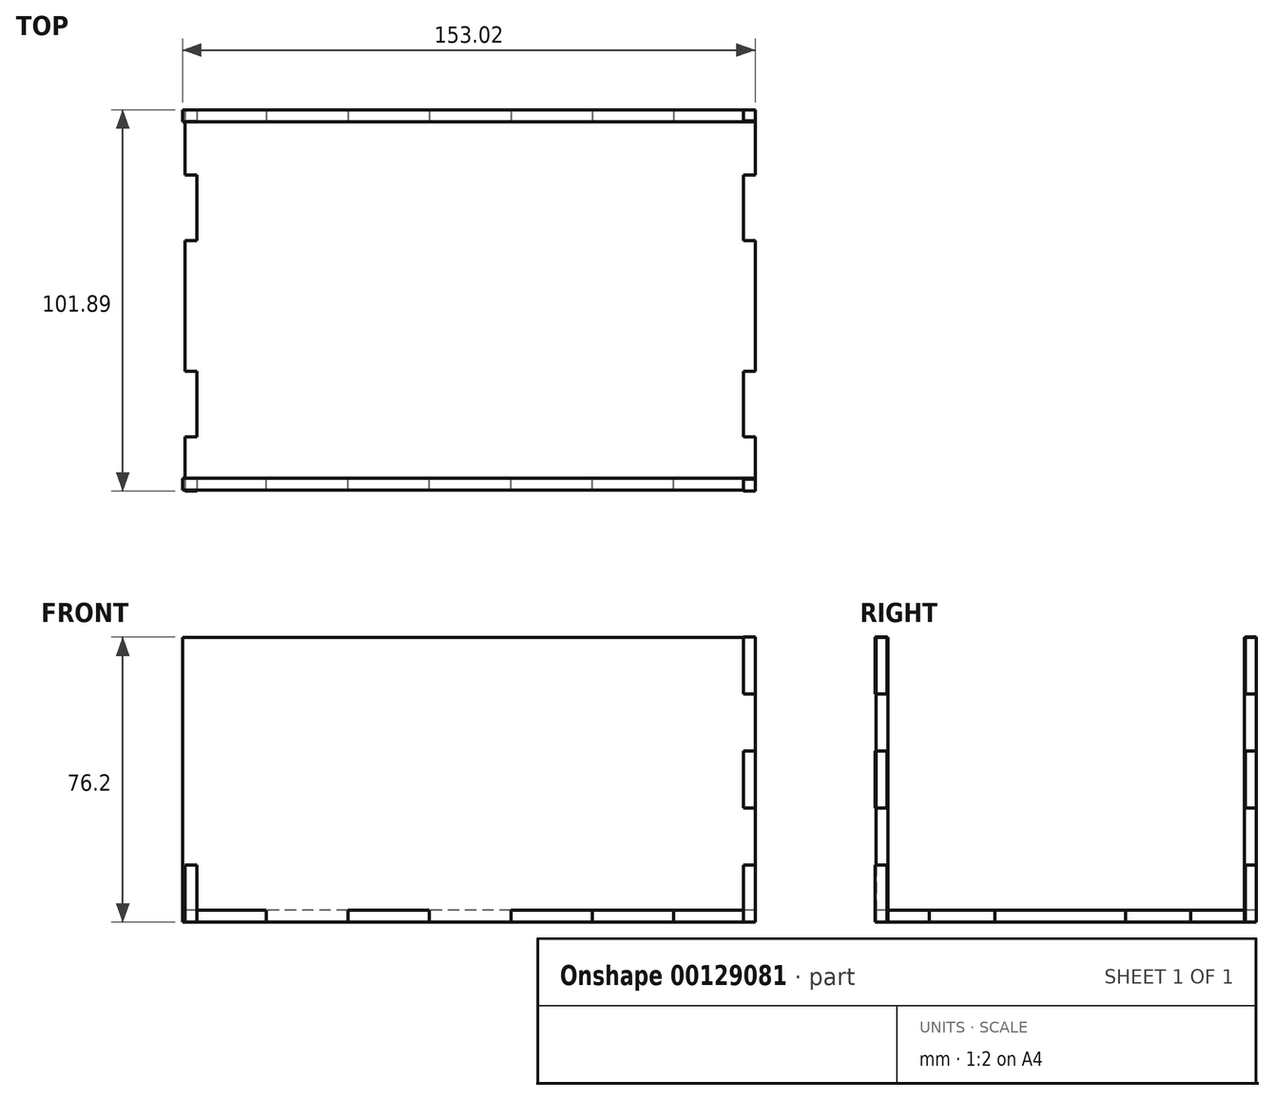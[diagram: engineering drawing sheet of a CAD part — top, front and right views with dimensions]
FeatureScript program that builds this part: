
annotation { "Feature Type Name" : "Feature", "Feature Type Description" : "" }
export const myFeature = defineFeature(function(context is Context, id is Id, definition is map)
    precondition{}
    {
        {
            var Q0;
            Q0=qCreatedBy(makeId("Top.planeOp"),FACE);
            var sketch = newSketch(context, id + "F0", { "sketchPlane" : qUnion([Q0])});
            skLineSegment(sketch, "E0.bottom", {"start": v(76.2, 50.8) * mm, "end": v(-76.2, 50.8) * mm});
            skLineSegment(sketch, "E0.top", {"start": v(76.2, -50.8) * mm, "end": v(-76.2, -50.8) * mm});
            skLineSegment(sketch, "E0.left", {"start": v(76.2, 50.8) * mm, "end": v(76.2, -50.8) * mm});
            skLineSegment(sketch, "E0.right", {"start": v(-76.2, 50.8) * mm, "end": v(-76.2, -50.8) * mm});
            skPoint(sketch, "E0.middle", {"position": v(0, 0) * mm});
            skLineSegment(sketch, "E1", {"start": v(-76.2, 50.8) * mm, "end": v(-73.03, 50.8) * mm});
            skLineSegment(sketch, "E2.0.1.0", {"start": v(-76.2, 33.33) * mm, "end": v(-73.03, 33.33) * mm});
            skLineSegment(sketch, "E2.0.2.0", {"start": v(-76.2, 15.85) * mm, "end": v(-73.03, 15.85) * mm});
            skLineSegment(sketch, "E2.0.3.0", {"start": v(-76.2, -1.62) * mm, "end": v(-73.03, -1.62) * mm});
            skLineSegment(sketch, "E2.0.4.0", {"start": v(-76.2, -19.1) * mm, "end": v(-73.03, -19.1) * mm});
            skLineSegment(sketch, "E2.0.5.0", {"start": v(-76.2, -36.57) * mm, "end": v(-73.02, -36.57) * mm});
            skLineSegment(sketch, "E2.direction1", {"start": v(-76.2, 50.8) * mm, "end": v(-50.8, 50.8) * mm, "construction": true});
            skLineSegment(sketch, "E2.direction2", {"start": v(-76.2, 50.8) * mm, "end": v(-76.2, 33.33) * mm, "construction": true});
            skLineSegment(sketch, "E3", {"start": v(-73.03, 50.8) * mm, "end": v(-73.03, -50.8) * mm});
            skLineSegment(sketch, "E4.MirrorCS", {"start": v(76.2, 50.8) * mm, "end": v(73.03, 50.8) * mm});
            skLineSegment(sketch, "E5.MirrorCS", {"start": v(76.2, 33.33) * mm, "end": v(73.03, 33.33) * mm});
            skLineSegment(sketch, "E6.MirrorCS", {"start": v(76.2, 15.85) * mm, "end": v(73.03, 15.85) * mm});
            skLineSegment(sketch, "E7.MirrorCS", {"start": v(76.2, -36.57) * mm, "end": v(73.02, -36.57) * mm});
            skLineSegment(sketch, "E8.MirrorCS", {"start": v(76.2, -1.62) * mm, "end": v(73.03, -1.62) * mm});
            skLineSegment(sketch, "E9.MirrorCS", {"start": v(76.2, -19.1) * mm, "end": v(73.03, -19.1) * mm});
            skLineSegment(sketch, "E10.MirrorCS", {"start": v(76.2, 50.8) * mm, "end": v(76.2, 33.33) * mm, "construction": true});
            skLineSegment(sketch, "E11.MirrorCS", {"start": v(73.03, 50.8) * mm, "end": v(73.03, -50.8) * mm});
            skLineSegment(sketch, "E12", {"start": v(-76.2, 50.8) * mm, "end": v(-76.2, 47.62) * mm});
            skLineSegment(sketch, "E13.1.0.0", {"start": v(-54.43, 50.8) * mm, "end": v(-54.43, 47.62) * mm});
            skLineSegment(sketch, "E13.2.0.0", {"start": v(-32.66, 50.8) * mm, "end": v(-32.66, 47.62) * mm});
            skLineSegment(sketch, "E13.3.0.0", {"start": v(-10.89, 50.8) * mm, "end": v(-10.89, 47.62) * mm});
            skLineSegment(sketch, "E13.4.0.0", {"start": v(10.89, 50.8) * mm, "end": v(10.89, 47.62) * mm});
            skLineSegment(sketch, "E13.5.0.0", {"start": v(32.66, 50.8) * mm, "end": v(32.66, 47.62) * mm});
            skLineSegment(sketch, "E13.6.0.0", {"start": v(54.43, 50.8) * mm, "end": v(54.43, 47.62) * mm});
            skLineSegment(sketch, "E13.7.0.0", {"start": v(76.2, 50.8) * mm, "end": v(76.2, 47.62) * mm});
            skLineSegment(sketch, "E13.direction1", {"start": v(-76.2, 47.62) * mm, "end": v(-54.43, 47.62) * mm, "construction": true});
            skLineSegment(sketch, "E14", {"start": v(-76.2, 47.62) * mm, "end": v(76.2, 47.62) * mm});
            skLineSegment(sketch, "E15.MirrorCS", {"start": v(-76.2, -50.8) * mm, "end": v(-73.03, -50.8) * mm});
            skLineSegment(sketch, "E16.MirrorCS", {"start": v(-76.2, -50.8) * mm, "end": v(-76.2, -47.62) * mm});
            skLineSegment(sketch, "E17.MirrorCS", {"start": v(76.2, -50.8) * mm, "end": v(76.2, -47.62) * mm});
            skLineSegment(sketch, "E18.MirrorCS", {"start": v(76.2, -50.8) * mm, "end": v(73.03, -50.8) * mm});
            skLineSegment(sketch, "E19.MirrorCS", {"start": v(-54.43, -50.8) * mm, "end": v(-54.43, -47.62) * mm});
            skLineSegment(sketch, "E20.MirrorCS", {"start": v(54.43, -50.8) * mm, "end": v(54.43, -47.62) * mm});
            skLineSegment(sketch, "E21.MirrorCS", {"start": v(-32.66, -50.8) * mm, "end": v(-32.66, -47.62) * mm});
            skLineSegment(sketch, "E22.MirrorCS", {"start": v(10.89, -50.8) * mm, "end": v(10.89, -47.62) * mm});
            skLineSegment(sketch, "E23.MirrorCS", {"start": v(32.66, -50.8) * mm, "end": v(32.66, -47.62) * mm});
            skLineSegment(sketch, "E24.MirrorCS", {"start": v(-10.89, -50.8) * mm, "end": v(-10.89, -47.62) * mm});
            skLineSegment(sketch, "E25.MirrorCS", {"start": v(-76.2, -47.62) * mm, "end": v(76.2, -47.62) * mm});
            skLineSegment(sketch, "E26.MirrorCS", {"start": v(-76.2, -47.62) * mm, "end": v(-54.43, -47.62) * mm, "construction": true});
            skLineSegment(sketch, "E27.MirrorCS", {"start": v(-76.2, -50.8) * mm, "end": v(-50.8, -50.8) * mm, "construction": true});
            skSolve(sketch);
        }
        {
            var Q0;
            {var subQ3=sQuery(id+"F0.wireOp",EDGE,"E13.1.0.0");Q0=makeQuery(id+"F0.imprint","IMPRINT",FACE,{"disambiguationData":[TD([[makeQuery(id+"F0.imprint","IMPRINT",EDGE,{"derivedFrom":subQ3}),-1.0]])]});}
            var Q1;
            {var subQ0=sQuery(id+"F0.wireOp",EDGE,"E1");Q1=makeQuery(id+"F0.imprint","IMPRINT",FACE,{"disambiguationData":[TD([[makeQuery(id+"F0.imprint","IMPRINT",EDGE,{"derivedFrom":subQ0}),-1.0]])]});}
            var Q2;
            {var subQ3=sQuery(id+"F0.wireOp",EDGE,"E2.0.1.0");Q2=makeQuery(id+"F0.imprint","IMPRINT",FACE,{"disambiguationData":[TD([[makeQuery(id+"F0.imprint","IMPRINT",EDGE,{"derivedFrom":subQ3}),1.0]])]});}
            var Q3;
            {var subQ0=sQuery(id+"F0.wireOp",EDGE,"E2.0.2.0");Q3=makeQuery(id+"F0.imprint","IMPRINT",FACE,{"disambiguationData":[TD([[makeQuery(id+"F0.imprint","IMPRINT",EDGE,{"derivedFrom":subQ0}),-1.0]])]});}
            var Q4;
            {var subQ0=sQuery(id+"F0.wireOp",EDGE,"E2.0.3.0");Q4=makeQuery(id+"F0.imprint","IMPRINT",FACE,{"disambiguationData":[TD([[makeQuery(id+"F0.imprint","IMPRINT",EDGE,{"derivedFrom":subQ0}),-1.0]])]});}
            var Q5;
            {var subQ3=sQuery(id+"F0.wireOp",EDGE,"E2.0.5.0");Q5=makeQuery(id+"F0.imprint","IMPRINT",FACE,{"disambiguationData":[TD([[makeQuery(id+"F0.imprint","IMPRINT",EDGE,{"derivedFrom":subQ3}),-1.0]])]});}
            var Q6;
            {var subQ5=sQuery(id+"F0.wireOp",EDGE,"E16.MirrorCS");Q6=makeQuery(id+"F0.imprint","IMPRINT",FACE,{"disambiguationData":[TD([[makeQuery(id+"F0.imprint","IMPRINT",EDGE,{"derivedFrom":subQ5}),-1.0]])]});}
            var Q7;
            {var subQ5=sQuery(id+"F0.wireOp",EDGE,"E19.MirrorCS");Q7=makeQuery(id+"F0.imprint","IMPRINT",FACE,{"disambiguationData":[TD([[makeQuery(id+"F0.imprint","IMPRINT",EDGE,{"derivedFrom":subQ5}),1.0]])]});}
            var Q8;
            {var subQ0=sQuery(id+"F0.wireOp",EDGE,"E21.MirrorCS");Q8=makeQuery(id+"F0.imprint","IMPRINT",FACE,{"disambiguationData":[TD([[makeQuery(id+"F0.imprint","IMPRINT",EDGE,{"derivedFrom":subQ0}),-1.0]])]});}
            var Q9;
            {var subQ0=sQuery(id+"F0.wireOp",EDGE,"E22.MirrorCS");Q9=makeQuery(id+"F0.imprint","IMPRINT",FACE,{"disambiguationData":[TD([[makeQuery(id+"F0.imprint","IMPRINT",EDGE,{"derivedFrom":subQ0}),-1.0]])]});}
            var Q10;
            {var subQ5=sQuery(id+"F0.wireOp",EDGE,"E20.MirrorCS");Q10=makeQuery(id+"F0.imprint","IMPRINT",FACE,{"disambiguationData":[TD([[makeQuery(id+"F0.imprint","IMPRINT",EDGE,{"derivedFrom":subQ5}),-1.0]])]});}
            var Q11;
            {var subQ0=sQuery(id+"F0.wireOp",EDGE,"E7.MirrorCS");Q11=makeQuery(id+"F0.imprint","IMPRINT",FACE,{"disambiguationData":[TD([[makeQuery(id+"F0.imprint","IMPRINT",EDGE,{"derivedFrom":subQ0}),1.0]])]});}
            var Q12;
            {var subQ0=sQuery(id+"F0.wireOp",EDGE,"E8.MirrorCS");Q12=makeQuery(id+"F0.imprint","IMPRINT",FACE,{"disambiguationData":[TD([[makeQuery(id+"F0.imprint","IMPRINT",EDGE,{"derivedFrom":subQ0}),1.0]])]});}
            var Q13;
            {var subQ0=sQuery(id+"F0.wireOp",EDGE,"E6.MirrorCS");Q13=makeQuery(id+"F0.imprint","IMPRINT",FACE,{"disambiguationData":[TD([[makeQuery(id+"F0.imprint","IMPRINT",EDGE,{"derivedFrom":subQ0}),1.0]])]});}
            var Q14;
            {var subQ0=sQuery(id+"F0.wireOp",EDGE,"E5.MirrorCS");Q14=makeQuery(id+"F0.imprint","IMPRINT",FACE,{"disambiguationData":[TD([[makeQuery(id+"F0.imprint","IMPRINT",EDGE,{"derivedFrom":subQ0}),-1.0]])]});}
            var Q15;
            {var subQ0=sQuery(id+"F0.wireOp",EDGE,"E4.MirrorCS");Q15=makeQuery(id+"F0.imprint","IMPRINT",FACE,{"disambiguationData":[TD([[makeQuery(id+"F0.imprint","IMPRINT",EDGE,{"derivedFrom":subQ0}),1.0]])]});}
            var Q16;
            {var subQ3=sQuery(id+"F0.wireOp",EDGE,"E13.6.0.0");Q16=makeQuery(id+"F0.imprint","IMPRINT",FACE,{"disambiguationData":[TD([[makeQuery(id+"F0.imprint","IMPRINT",EDGE,{"derivedFrom":subQ3}),1.0]])]});}
            var Q17;
            {var subQ0=sQuery(id+"F0.wireOp",EDGE,"E13.4.0.0");Q17=makeQuery(id+"F0.imprint","IMPRINT",FACE,{"disambiguationData":[TD([[makeQuery(id+"F0.imprint","IMPRINT",EDGE,{"derivedFrom":subQ0}),1.0]])]});}
            var Q18;
            {var subQ0=sQuery(id+"F0.wireOp",EDGE,"E13.2.0.0");Q18=makeQuery(id+"F0.imprint","IMPRINT",FACE,{"disambiguationData":[TD([[makeQuery(id+"F0.imprint","IMPRINT",EDGE,{"derivedFrom":subQ0}),1.0]])]});}
            var Q19;
            {var subQ6=sQuery(id+"F0.wireOp",EDGE,"E3");var subQ25=makeQuery(id+"F0.imprint","INTERSECT",VERTEX,{"derivedFrom":[sQuery(id+"F0.wireOp",EDGE,"E2.0.1.0"),subQ6]});Q19=makeQuery(id+"F0.imprint","IMPRINT",FACE,{"disambiguationData":[TD([[makeQuery(id+"F0.imprint","IMPRINT",EDGE,{"disambiguationData":[TD([[subQ25,1.0]])],"derivedFrom":subQ6}),1.0]])]});}
            extrude(context, id + "F1", {"entities" : qUnion([Q0, Q1, Q2, Q3, Q4, Q5, Q6, Q7, Q8, Q9, Q10, Q11, Q12, Q13, Q14, Q15, Q16, Q17, Q18, Q19]), "depth" : 3.17 * mm});
        }
        {
            var Q0;
            {var subQ0=sQuery(id+"F0.wireOp",EDGE,"E0.left");Q0=makeQuery(id+"F1.opExtrude","SWEPT_FACE",FACE,{"disambiguationData":[OSD([subQ0]),TDD([makeQuery(id+"F0.imprint","IMPRINT",EDGE,{"disambiguationData":[TD([[makeQuery(id+"F0.imprint","INTERSECT",VERTEX,{"derivedFrom":[sQuery(id+"F0.wireOp",EDGE,"E7.MirrorCS"),subQ0]}),-1.0]])],"derivedFrom":subQ0})])]});}
            var sketch = newSketch(context, id + "F2", { "sketchPlane" : qUnion([Q0])});
            skLineSegment(sketch, "E28.bottom", {"start": v(50.8, 0) * mm, "end": v(-51.09, 0) * mm});
            skLineSegment(sketch, "E28.top", {"start": v(50.8, 76.2) * mm, "end": v(-51.09, 76.2) * mm});
            skLineSegment(sketch, "E28.left", {"start": v(50.8, 0) * mm, "end": v(50.8, 76.2) * mm});
            skLineSegment(sketch, "E28.right", {"start": v(-51.09, 0) * mm, "end": v(-51.09, 76.2) * mm});
            skLineSegment(sketch, "E29", {"start": v(-51.09, 76.2) * mm, "end": v(-47.91, 76.2) * mm});
            skLineSegment(sketch, "E30.0.1.0", {"start": v(-51.09, 60.96) * mm, "end": v(-47.91, 60.96) * mm});
            skLineSegment(sketch, "E30.0.2.0", {"start": v(-51.09, 45.72) * mm, "end": v(-47.91, 45.72) * mm});
            skLineSegment(sketch, "E30.0.3.0", {"start": v(-51.09, 30.48) * mm, "end": v(-47.91, 30.48) * mm});
            skLineSegment(sketch, "E30.0.4.0", {"start": v(-51.09, 15.24) * mm, "end": v(-47.91, 15.24) * mm});
            skLineSegment(sketch, "E30.0.5.0", {"start": v(-51.09, 0) * mm, "end": v(-47.91, 0) * mm});
            skLineSegment(sketch, "E30.direction1", {"start": v(-51.09, 76.2) * mm, "end": v(-25.69, 76.2) * mm, "construction": true});
            skLineSegment(sketch, "E30.direction2", {"start": v(-51.09, 76.2) * mm, "end": v(-51.09, 60.96) * mm, "construction": true});
            skLineSegment(sketch, "E31", {"start": v(-47.91, 0) * mm, "end": v(-47.91, 76.2) * mm});
            skLineSegment(sketch, "E32.MirrorCS", {"start": v(51.09, 76.2) * mm, "end": v(47.91, 76.2) * mm});
            skLineSegment(sketch, "E33.MirrorCS", {"start": v(51.09, 0) * mm, "end": v(47.91, 0) * mm});
            skLineSegment(sketch, "E34.MirrorCS", {"start": v(51.09, 45.72) * mm, "end": v(47.91, 45.72) * mm});
            skLineSegment(sketch, "E35.MirrorCS", {"start": v(51.09, 60.96) * mm, "end": v(47.91, 60.96) * mm});
            skLineSegment(sketch, "E36.MirrorCS", {"start": v(51.09, 30.48) * mm, "end": v(47.91, 30.48) * mm});
            skLineSegment(sketch, "E37.MirrorCS", {"start": v(51.09, 15.24) * mm, "end": v(47.91, 15.24) * mm});
            skLineSegment(sketch, "E38.MirrorCS", {"start": v(51.09, 0) * mm, "end": v(51.09, 76.2) * mm});
            skLineSegment(sketch, "E39.MirrorCS", {"start": v(47.91, 0) * mm, "end": v(47.91, 76.2) * mm});
            skLineSegment(sketch, "E40.MirrorCS", {"start": v(51.09, 76.2) * mm, "end": v(51.09, 60.96) * mm, "construction": true});
            skSolve(sketch);
        }
        {
            var Q0;
            {var subQ0=sQuery(id+"F2.wireOp",EDGE,"E29");Q0=makeQuery(id+"F2.imprint","IMPRINT",FACE,{"disambiguationData":[TD([[makeQuery(id+"F2.imprint","IMPRINT",EDGE,{"derivedFrom":subQ0}),-1.0]])]});}
            var Q1;
            {var subQ0=sQuery(id+"F2.wireOp",EDGE,"E30.0.2.0");Q1=makeQuery(id+"F2.imprint","IMPRINT",FACE,{"disambiguationData":[TD([[makeQuery(id+"F2.imprint","IMPRINT",EDGE,{"derivedFrom":subQ0}),-1.0]])]});}
            var Q2;
            {var subQ2=sQuery(id+"F2.wireOp",EDGE,"E30.0.4.0");Q2=makeQuery(id+"F2.imprint","IMPRINT",FACE,{"disambiguationData":[TD([[makeQuery(id+"F2.imprint","IMPRINT",EDGE,{"derivedFrom":subQ2}),-1.0]])]});}
            var Q3;
            {var subQ0=sQuery(id+"F2.wireOp",EDGE,"E36.MirrorCS");var subQ1=sQuery(id+"F2.wireOp",EDGE,"E28.left");var subQ2=makeQuery(id+"F2.imprint","INTERSECT",VERTEX,{"derivedFrom":[subQ1,subQ0]});Q3=makeQuery(id+"F2.imprint","IMPRINT",FACE,{"disambiguationData":[TD([[makeQuery(id+"F2.imprint","IMPRINT",EDGE,{"disambiguationData":[TD([[subQ2,-1.0]])],"derivedFrom":subQ1}),1.0]])]});}
            var Q4;
            {var subQ0=sQuery(id+"F2.wireOp",EDGE,"E33.MirrorCS");var subQ1=sQuery(id+"F2.wireOp",EDGE,"E28.left");var subQ2=makeQuery(id+"F2.imprint","INTERSECT",VERTEX,{"derivedFrom":[subQ1,subQ0]});Q4=makeQuery(id+"F2.imprint","IMPRINT",FACE,{"disambiguationData":[TD([[makeQuery(id+"F2.imprint","IMPRINT",EDGE,{"disambiguationData":[TD([[subQ2,-1.0]])],"derivedFrom":subQ1}),1.0]])]});}
            var Q5;
            {var subQ0=sQuery(id+"F2.wireOp",EDGE,"E32.MirrorCS");var subQ1=sQuery(id+"F2.wireOp",EDGE,"E28.left");var subQ2=makeQuery(id+"F2.imprint","INTERSECT",VERTEX,{"derivedFrom":[subQ1,subQ0]});Q5=makeQuery(id+"F2.imprint","IMPRINT",FACE,{"disambiguationData":[TD([[makeQuery(id+"F2.imprint","IMPRINT",EDGE,{"disambiguationData":[TD([[subQ2,1.0]])],"derivedFrom":subQ1}),1.0]])]});}
            var Q6;
            {var subQ4=sQuery(id+"F2.wireOp",EDGE,"E28.top");Q6=makeQuery(id+"F2.imprint","IMPRINT",FACE,{"disambiguationData":[TD([[makeQuery(id+"F2.imprint","IMPRINT",EDGE,{"derivedFrom":subQ4}),1.0]])]});}
            extrude(context, id + "F3", {"entities" : qUnion([Q0, Q1, Q2, Q3, Q4, Q5, Q6]), "operationType" : NewBodyOperationType.ADD, "oppositeDirection" : true, "depth" : 3.17 * mm});
        }
        {
            var Q0;
            Q0=makeQuery(id+"F1.opExtrude","SWEPT_BODY",BODY,{"disambiguationData":[OSD([sQuery(id+"F0.wireOp",EDGE,"E0.bottom"),sQuery(id+"F0.wireOp",EDGE,"E0.right"),sQuery(id+"F0.wireOp",EDGE,"E1"),sQuery(id+"F0.wireOp",EDGE,"E2.0.1.0"),sQuery(id+"F0.wireOp",EDGE,"E2.0.2.0"),sQuery(id+"F0.wireOp",EDGE,"E2.0.4.0"),sQuery(id+"F0.wireOp",EDGE,"E2.0.5.0"),sQuery(id+"F0.wireOp",EDGE,"E3"),sQuery(id+"F0.wireOp",EDGE,"E4.MirrorCS"),sQuery(id+"F0.wireOp",EDGE,"E5.MirrorCS"),sQuery(id+"F0.wireOp",EDGE,"E6.MirrorCS"),sQuery(id+"F0.wireOp",EDGE,"E7.MirrorCS"),sQuery(id+"F0.wireOp",EDGE,"E9.MirrorCS"),sQuery(id+"F0.wireOp",EDGE,"E0.left"),sQuery(id+"F0.wireOp",EDGE,"E11.MirrorCS"),sQuery(id+"F0.wireOp",EDGE,"E12"),sQuery(id+"F0.wireOp",EDGE,"E13.1.0.0"),sQuery(id+"F0.wireOp",EDGE,"E13.2.0.0"),sQuery(id+"F0.wireOp",EDGE,"E13.3.0.0"),sQuery(id+"F0.wireOp",EDGE,"E13.4.0.0"),sQuery(id+"F0.wireOp",EDGE,"E13.5.0.0"),sQuery(id+"F0.wireOp",EDGE,"E13.6.0.0"),sQuery(id+"F0.wireOp",EDGE,"E13.7.0.0"),sQuery(id+"F0.wireOp",EDGE,"E14"),sQuery(id+"F0.wireOp",EDGE,"E16.MirrorCS"),sQuery(id+"F0.wireOp",EDGE,"E19.MirrorCS"),sQuery(id+"F0.wireOp",EDGE,"E20.MirrorCS"),sQuery(id+"F0.wireOp",EDGE,"E21.MirrorCS"),sQuery(id+"F0.wireOp",EDGE,"E22.MirrorCS"),sQuery(id+"F0.wireOp",EDGE,"E23.MirrorCS"),sQuery(id+"F0.wireOp",EDGE,"E24.MirrorCS"),sQuery(id+"F0.wireOp",EDGE,"E25.MirrorCS"),sQuery(id+"F0.wireOp",EDGE,"E0.top")])]});
            var Q1;
            Q1=qCreatedBy(makeId("Right.planeOp"),FACE);
            mirror(context, id + "F4", {"entities" : qUnion([Q0]), "mirrorPlane" : qUnion([Q1])});
        }
        {
            var Q0;
            {var subQ0=sQuery(id+"F0.wireOp",EDGE,"E14");Q0=makeQuery(id+"F4.opPattern","COPY",FACE,{"derivedFrom":makeQuery(id+"F1.opExtrude","SWEPT_FACE",FACE,{"disambiguationData":[OSD([subQ0]),TDD([makeQuery(id+"F0.imprint","IMPRINT",EDGE,{"disambiguationData":[TD([[makeQuery(id+"F0.imprint","INTERSECT",VERTEX,{"derivedFrom":[sQuery(id+"F0.wireOp",EDGE,"E13.1.0.0"),subQ0]}),-1.0]])],"derivedFrom":subQ0})])]}),"instanceName":"1"});}
            var sketch = newSketch(context, id + "F5", { "sketchPlane" : qUnion([Q0])});
            skLineSegment(sketch, "E41.bottom", {"start": v(-76.2, 0) * mm, "end": v(76.82, 0) * mm});
            skLineSegment(sketch, "E41.top", {"start": v(-76.2, 76.14) * mm, "end": v(76.82, 76.14) * mm});
            skLineSegment(sketch, "E41.left", {"start": v(-76.2, 0) * mm, "end": v(-76.2, 76.14) * mm});
            skLineSegment(sketch, "E41.right", {"start": v(76.82, 0) * mm, "end": v(76.82, 76.14) * mm});
            skSolve(sketch);
        }
        {
            var Q0;
            Q0=makeQuery(id+"F5.imprint","IMPRINT",FACE,{"disambiguationData":[TD([[makeQuery(id+"F5.imprint","IMPRINT",EDGE,{"derivedFrom":sQuery(id+"F5.wireOp",EDGE,"E41.top")}),-1.0]])]});
            extrude(context, id + "F6", {"entities" : qUnion([Q0]), "depth" : 3.17 * mm});
        }
        {
            var Q0;
            Q0=makeQuery(id+"F6.opExtrude","SWEPT_BODY",BODY,{"disambiguationData":[OSD([sQuery(id+"F0.wireOp",EDGE,"E13.1.0.0"),sQuery(id+"F0.wireOp",EDGE,"E13.2.0.0"),sQuery(id+"F0.wireOp",EDGE,"E14"),sQuery(id+"F5.wireOp",EDGE,"E41.bottom"),sQuery(id+"F5.wireOp",EDGE,"E41.top"),sQuery(id+"F5.wireOp",EDGE,"E41.left"),sQuery(id+"F5.wireOp",EDGE,"E41.right")])]});
            var Q1;
            Q1=qCreatedBy(makeId("Front.planeOp"),FACE);
            mirror(context, id + "F7", {"entities" : qUnion([Q0]), "mirrorPlane" : qUnion([Q1])});
        }
        {
            var Q0;
            Q0=makeQuery(id+"F1.opExtrude","SWEPT_BODY",BODY,{"disambiguationData":[OSD([sQuery(id+"F0.wireOp",EDGE,"E0.bottom"),sQuery(id+"F0.wireOp",EDGE,"E0.right"),sQuery(id+"F0.wireOp",EDGE,"E1"),sQuery(id+"F0.wireOp",EDGE,"E2.0.1.0"),sQuery(id+"F0.wireOp",EDGE,"E2.0.2.0"),sQuery(id+"F0.wireOp",EDGE,"E2.0.4.0"),sQuery(id+"F0.wireOp",EDGE,"E2.0.5.0"),sQuery(id+"F0.wireOp",EDGE,"E3"),sQuery(id+"F0.wireOp",EDGE,"E4.MirrorCS"),sQuery(id+"F0.wireOp",EDGE,"E5.MirrorCS"),sQuery(id+"F0.wireOp",EDGE,"E6.MirrorCS"),sQuery(id+"F0.wireOp",EDGE,"E7.MirrorCS"),sQuery(id+"F0.wireOp",EDGE,"E9.MirrorCS"),sQuery(id+"F0.wireOp",EDGE,"E0.left"),sQuery(id+"F0.wireOp",EDGE,"E11.MirrorCS"),sQuery(id+"F0.wireOp",EDGE,"E12"),sQuery(id+"F0.wireOp",EDGE,"E13.1.0.0"),sQuery(id+"F0.wireOp",EDGE,"E13.2.0.0"),sQuery(id+"F0.wireOp",EDGE,"E13.3.0.0"),sQuery(id+"F0.wireOp",EDGE,"E13.4.0.0"),sQuery(id+"F0.wireOp",EDGE,"E13.5.0.0"),sQuery(id+"F0.wireOp",EDGE,"E13.6.0.0"),sQuery(id+"F0.wireOp",EDGE,"E13.7.0.0"),sQuery(id+"F0.wireOp",EDGE,"E14"),sQuery(id+"F0.wireOp",EDGE,"E16.MirrorCS"),sQuery(id+"F0.wireOp",EDGE,"E19.MirrorCS"),sQuery(id+"F0.wireOp",EDGE,"E20.MirrorCS"),sQuery(id+"F0.wireOp",EDGE,"E21.MirrorCS"),sQuery(id+"F0.wireOp",EDGE,"E22.MirrorCS"),sQuery(id+"F0.wireOp",EDGE,"E23.MirrorCS"),sQuery(id+"F0.wireOp",EDGE,"E24.MirrorCS"),sQuery(id+"F0.wireOp",EDGE,"E25.MirrorCS"),sQuery(id+"F0.wireOp",EDGE,"E0.top")])]});
            var Q1;
            Q1=makeQuery(id+"F4.opPattern","COPY",BODY,{"derivedFrom":makeQuery(id+"F1.opExtrude","SWEPT_BODY",BODY,{"disambiguationData":[OSD([sQuery(id+"F0.wireOp",EDGE,"E0.bottom"),sQuery(id+"F0.wireOp",EDGE,"E0.right"),sQuery(id+"F0.wireOp",EDGE,"E1"),sQuery(id+"F0.wireOp",EDGE,"E2.0.1.0"),sQuery(id+"F0.wireOp",EDGE,"E2.0.2.0"),sQuery(id+"F0.wireOp",EDGE,"E2.0.4.0"),sQuery(id+"F0.wireOp",EDGE,"E2.0.5.0"),sQuery(id+"F0.wireOp",EDGE,"E3"),sQuery(id+"F0.wireOp",EDGE,"E4.MirrorCS"),sQuery(id+"F0.wireOp",EDGE,"E5.MirrorCS"),sQuery(id+"F0.wireOp",EDGE,"E6.MirrorCS"),sQuery(id+"F0.wireOp",EDGE,"E7.MirrorCS"),sQuery(id+"F0.wireOp",EDGE,"E9.MirrorCS"),sQuery(id+"F0.wireOp",EDGE,"E0.left"),sQuery(id+"F0.wireOp",EDGE,"E11.MirrorCS"),sQuery(id+"F0.wireOp",EDGE,"E12"),sQuery(id+"F0.wireOp",EDGE,"E13.1.0.0"),sQuery(id+"F0.wireOp",EDGE,"E13.2.0.0"),sQuery(id+"F0.wireOp",EDGE,"E13.3.0.0"),sQuery(id+"F0.wireOp",EDGE,"E13.4.0.0"),sQuery(id+"F0.wireOp",EDGE,"E13.5.0.0"),sQuery(id+"F0.wireOp",EDGE,"E13.6.0.0"),sQuery(id+"F0.wireOp",EDGE,"E13.7.0.0"),sQuery(id+"F0.wireOp",EDGE,"E14"),sQuery(id+"F0.wireOp",EDGE,"E16.MirrorCS"),sQuery(id+"F0.wireOp",EDGE,"E19.MirrorCS"),sQuery(id+"F0.wireOp",EDGE,"E20.MirrorCS"),sQuery(id+"F0.wireOp",EDGE,"E21.MirrorCS"),sQuery(id+"F0.wireOp",EDGE,"E22.MirrorCS"),sQuery(id+"F0.wireOp",EDGE,"E23.MirrorCS"),sQuery(id+"F0.wireOp",EDGE,"E24.MirrorCS"),sQuery(id+"F0.wireOp",EDGE,"E25.MirrorCS"),sQuery(id+"F0.wireOp",EDGE,"E0.top")])]}),"instanceName":"1"});
            var Q2;
            Q2=makeQuery(id+"F6.opExtrude","SWEPT_BODY",BODY,{"disambiguationData":[OSD([sQuery(id+"F0.wireOp",EDGE,"E13.1.0.0"),sQuery(id+"F0.wireOp",EDGE,"E13.2.0.0"),sQuery(id+"F0.wireOp",EDGE,"E14"),sQuery(id+"F5.wireOp",EDGE,"E41.bottom"),sQuery(id+"F5.wireOp",EDGE,"E41.top"),sQuery(id+"F5.wireOp",EDGE,"E41.left"),sQuery(id+"F5.wireOp",EDGE,"E41.right")])]});
            var Q3;
            Q3=makeQuery(id+"F7.opPattern","COPY",BODY,{"derivedFrom":makeQuery(id+"F6.opExtrude","SWEPT_BODY",BODY,{"disambiguationData":[OSD([sQuery(id+"F0.wireOp",EDGE,"E13.1.0.0"),sQuery(id+"F0.wireOp",EDGE,"E13.2.0.0"),sQuery(id+"F0.wireOp",EDGE,"E14"),sQuery(id+"F5.wireOp",EDGE,"E41.bottom"),sQuery(id+"F5.wireOp",EDGE,"E41.top"),sQuery(id+"F5.wireOp",EDGE,"E41.left"),sQuery(id+"F5.wireOp",EDGE,"E41.right")])]}),"instanceName":"1"});
            booleanBodies(context, id + "F8", {"operationType" : BooleanOperationType.SUBTRACTION, "tools" : qUnion([Q0, Q1]), "targets" : qUnion([Q2, Q3]), "keepTools" : true});
        }
    });
